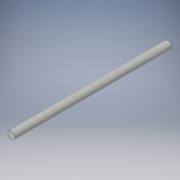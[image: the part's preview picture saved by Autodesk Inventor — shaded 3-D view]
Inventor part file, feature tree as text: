
AUTODESK INVENTOR PART (.ipt)
format: ipt  version: 2016 (Build 200138000, 138)  size: 88,064 bytes
history: native  units: in
note: dims shown in document units (in); Inventor stores cm internally (conversion verified against a paired STEP export)
features: extrude x1, plane x1, sketch x1
ambient origin geometry x8: Origin, YZ Plane, XZ Plane, XY Plane, X Axis, Y Axis, Z Axis, Center Point
bodies: Solid1 (feature_tree)
feature tree (3):
  extrude  "Extrusion1"  Depth=16.0in TaperAngle=0.0deg
  plane  "Work Plane1"
  sketch  "Sketch1"  dims[d0=0.75in d1=16.0in d2=0.0in d3=0.375in]
